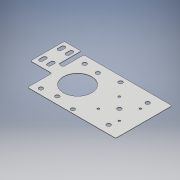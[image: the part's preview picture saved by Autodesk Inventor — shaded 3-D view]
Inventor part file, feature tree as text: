
AUTODESK INVENTOR PART (.ipt)
format: ipt  version: 2018 (Build 220112000, 112)  size: 192,000 bytes
history: native  units: mm
features: extrude x1, fillet x1, sketch x1
ambient origin geometry x8: Origin, YZ Plane, XZ Plane, XY Plane, X Axis, Y Axis, Z Axis, Center Point
bodies: Body1 (feature_tree)
feature tree (3):
  extrude  "Extrusión2"  Depth=130.29mm
  fillet  "Empalme2"  Radius=37.46mm
  sketch  "Boceto1"  dims[d0=245.51mm d1=130.29mm d2=37.46mm d3=75.73mm d18=5.0mm d19=5.0mm d20=5.0mm d21=5.0mm d27=9.0mm d28=9.0mm d29=9.0mm d34=9.0mm d35=9.0mm d40=9.0mm d41=9.0mm d45=9.0mm d46=9.0mm d47=63.51mm d94=0.8mm d95=0.0mm d97=3.0mm d76=1.0mm d77=1.0mm]
